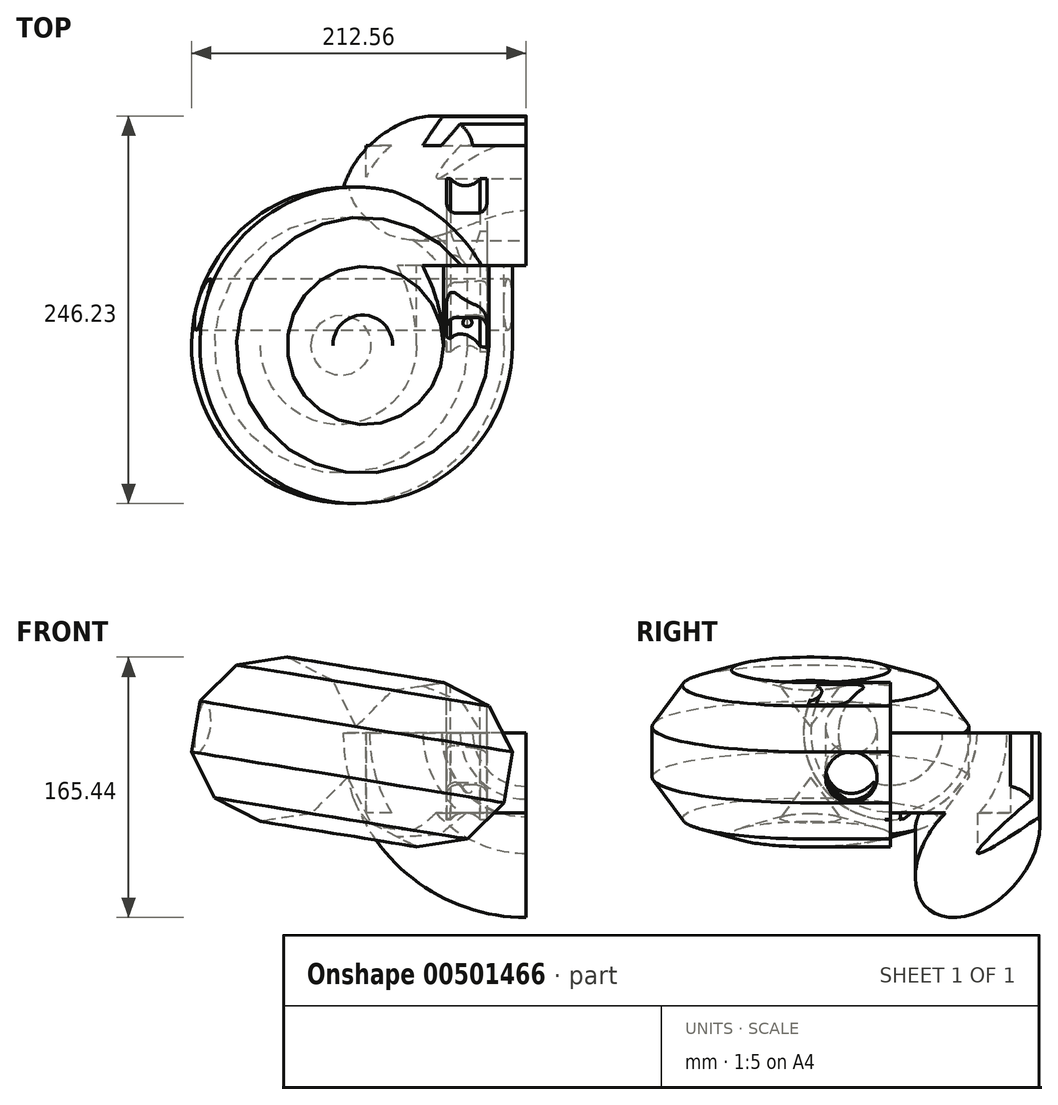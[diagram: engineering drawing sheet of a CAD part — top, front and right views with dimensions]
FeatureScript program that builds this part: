
annotation { "Feature Type Name" : "Feature", "Feature Type Description" : "" }
export const myFeature = defineFeature(function(context is Context, id is Id, definition is map)
    precondition{}
    {
        {
            var Q0;
            Q0=qCreatedBy(makeId("Right.planeOp"),FACE);
            var sketch = newSketch(context, id + "F0", { "sketchPlane" : qUnion([Q0])});
            skLineSegment(sketch, "E0.bottom", {"start": v(0, 50.8) * mm, "end": v(76.2, 50.8) * mm});
            skLineSegment(sketch, "E0.top", {"start": v(0, 0) * mm, "end": v(76.2, 0) * mm});
            skLineSegment(sketch, "E0.left", {"start": v(0, 50.8) * mm, "end": v(0, 0) * mm});
            skLineSegment(sketch, "E0.right", {"start": v(76.2, 50.8) * mm, "end": v(76.2, 0) * mm});
            skSolve(sketch);
        }
        {
            var Q0;
            Q0 = qSketchRegion(id + "F0", true);
            extrude(context, id + "F1", {"entities" : qUnion([Q0]), "depth" : 101.6 * mm});
        }
        {
            var Q0;
            Q0=makeQuery(id+"F1.opExtrude","CAP_FACE",FACE,{"disambiguationData":[OSD([sQuery(id+"F0.wireOp",EDGE,"E0.bottom"),sQuery(id+"F0.wireOp",EDGE,"E0.top"),sQuery(id+"F0.wireOp",EDGE,"E0.left"),sQuery(id+"F0.wireOp",EDGE,"E0.right")])],"isStart":false});
            var sketch = newSketch(context, id + "F2", { "sketchPlane" : qUnion([Q0])});
            skEllipticalArc(sketch, "E1", {});
            skEllipticalArc(sketch, "E2", {});
            skPoint(sketch, "E2.centerSnap0", {"position": v(55.38, -25.47) * mm});
            const initialGuessF2  = {"E1": [0.1582920104265213, 0.054269641637802124, -0.7904881080216445, -0.6124773882163822, 0.13018475622554335, 0.007689410792664507, 5.394513098691121, 0.8567772667814274], "E2": [0.05538250878453253, -0.0245770997165353, 0.6531900166199548, 0.7571940320604906, 0.048106603113153935, 0.03167227913565867, 6.147645044378101, 5.782845178718024]};
            skSetInitialGuess(sketch, initialGuessF2);
            skSolve(sketch);
        }
        {
            var Q0;
            {var subQ1=sQuery(id+"F2.wireOp",EDGE,"E1");Q0=makeQuery(id+"F2.imprint","IMPRINT",FACE,{"disambiguationData":[TD([[makeQuery(id+"F2.imprint","IMPRINT",EDGE,{"derivedFrom":subQ1}),-1.0]])]});}
            var Q1;
            Q1=makeQuery(id+"F1.opExtrude","CAP_EDGE",EDGE,{"disambiguationData":[OSD([sQuery(id+"F0.wireOp",EDGE,"E0.bottom")])],"isStart":false});
            revolve(context, id + "F3", {"operationType" : NewBodyOperationType.ADD, "entities" : qUnion([Q0]), "axis" : qUnion([Q1]), "revolveType" : RevolveType.ONE_DIRECTION, "angle" : 90 * degree});
        }
        {
            var Q0;
            Q0=makeQuery(id+"F1.opExtrude","SWEPT_FACE",FACE,{"disambiguationData":[OSD([sQuery(id+"F0.wireOp",EDGE,"E0.left")])]});
            var sketch = newSketch(context, id + "F4", { "sketchPlane" : qUnion([Q0])});
            skCircle(sketch, "E3.cCircle", {"center": v(40.49, 30.66) * mm, "radius": 52.85 * mm, "construction": true});
            skLineSegment(sketch, "E3.0", {"start": v(32, -21.5) * mm, "end": v(2.96, -6.55) * mm});
            skLineSegment(sketch, "E3.1", {"start": v(2.96, -6.55) * mm, "end": v(-11.74, 22.61) * mm});
            skLineSegment(sketch, "E3.2", {"start": v(-11.74, 22.61) * mm, "end": v(-6.5, 54.85) * mm});
            skLineSegment(sketch, "E3.3", {"start": v(-6.5, 54.85) * mm, "end": v(16.7, 77.85) * mm});
            skLineSegment(sketch, "E3.4", {"start": v(16.7, 77.85) * mm, "end": v(48.98, 82.82) * mm});
            skLineSegment(sketch, "E3.5", {"start": v(48.98, 82.82) * mm, "end": v(78.02, 67.87) * mm});
            skLineSegment(sketch, "E3.6", {"start": v(78.02, 67.87) * mm, "end": v(92.72, 38.7) * mm});
            skLineSegment(sketch, "E3.7", {"start": v(92.72, 38.7) * mm, "end": v(87.47, 6.46) * mm});
            skLineSegment(sketch, "E3.8", {"start": v(87.47, 6.46) * mm, "end": v(64.28, -16.53) * mm});
            skLineSegment(sketch, "E3.9", {"start": v(64.28, -16.53) * mm, "end": v(32, -21.5) * mm});
            skSolve(sketch);
        }
        {
            var Q0;
            Q0 = qSketchRegion(id + "F4", true);
            extrude(context, id + "F5", {"entities" : qUnion([Q0]), "operationType" : NewBodyOperationType.ADD, "depth" : 50.8 * mm});
        }
        {
            var Q0;
            Q0=makeQuery(id+"F5.opExtrude","CAP_FACE",FACE,{"disambiguationData":[OSD([sQuery(id+"F4.wireOp",EDGE,"E3.0"),sQuery(id+"F4.wireOp",EDGE,"E3.1"),sQuery(id+"F4.wireOp",EDGE,"E3.2"),sQuery(id+"F4.wireOp",EDGE,"E3.3"),sQuery(id+"F4.wireOp",EDGE,"E3.4"),sQuery(id+"F4.wireOp",EDGE,"E3.5"),sQuery(id+"F4.wireOp",EDGE,"E3.6"),sQuery(id+"F4.wireOp",EDGE,"E3.7"),sQuery(id+"F4.wireOp",EDGE,"E3.8"),sQuery(id+"F4.wireOp",EDGE,"E3.9")])],"isStart":false});
            var Q1;
            Q1=makeQuery(id+"F5.opExtrude","CAP_EDGE",EDGE,{"disambiguationData":[OSD([sQuery(id+"F4.wireOp",EDGE,"E3.2")])],"isStart":false});
            revolve(context, id + "F6", {"operationType" : NewBodyOperationType.ADD, "entities" : qUnion([Q0]), "axis" : qUnion([Q1]), "revolveType" : RevolveType.FULL});
        }
        {
            var Q0;
            Q0=makeQuery(id+"F5.opExtrude","SWEPT_FACE",FACE,{"disambiguationData":[OSD([sQuery(id+"F4.wireOp",EDGE,"E3.7")])]});
            var sketch = newSketch(context, id + "F7", { "sketchPlane" : qUnion([Q0])});
            skCircle(sketch, "E4", {"center": v(-24.83, 36.76) * mm, "radius": 16.33 * mm});
            skSolve(sketch);
        }
        {
            var Q0;
            Q0 = qSketchRegion(id + "F7", true);
            extrude(context, id + "F8", {"entities" : qUnion([Q0]), "operationType" : NewBodyOperationType.REMOVE, "endBound" : BoundingType.THROUGH_ALL, "oppositeDirection" : true, "depth" : 25.4 * mm});
        }
        {
            var Q0;
            Q0=makeQuery(id+"F3.boolean.opBoolean","MERGE",FACE,{"derivedFrom":[makeQuery(id+"F1.opExtrude","SWEPT_FACE",FACE,{"disambiguationData":[OSD([sQuery(id+"F0.wireOp",EDGE,"E0.bottom")])]}),makeQuery(id+"F3.opRevolve","CAP_FACE",FACE,{"disambiguationData":[OSD([sQuery(id+"F0.wireOp",EDGE,"E0.top"),sQuery(id+"F0.wireOp",EDGE,"E0.right"),sQuery(id+"F2.wireOp",EDGE,"E1"),sQuery(id+"F2.wireOp",EDGE,"E2")])],"isStart":false})]});
            var sketch = newSketch(context, id + "F9", { "sketchPlane" : qUnion([Q0])});
            skLineSegment(sketch, "E5.bottom", {"start": v(70.31, 33.13) * mm, "end": v(57.4, 33.13) * mm});
            skLineSegment(sketch, "E5.top", {"start": v(76.66, 55.18) * mm, "end": v(72.33, 55.18) * mm});
            skLineSegment(sketch, "E5.left", {"start": v(76.66, 39.48) * mm, "end": v(76.66, 55.18) * mm});
            skLineSegment(sketch, "E5.right", {"start": v(51.04, 39.48) * mm, "end": v(51.04, 55.18) * mm});
            skArc(sketch, "E6", {"start": v(53.65, 55.18) * mm, "mid": v(62.99, 50.56) * mm, "end": v(72.33, 55.18) * mm});
            skPoint(sketch, "E7.visualSharp", {"position": v(51.04, 33.13) * mm});
            skArc(sketch, "E7.filletArc", {"start": v(51.04, 39.48) * mm, "mid": v(52.9, 35) * mm, "end": v(57.4, 33.13) * mm});
            skPoint(sketch, "E8.visualSharp", {"position": v(76.66, 33.13) * mm});
            skArc(sketch, "E8.filletArc", {"start": v(70.31, 33.13) * mm, "mid": v(74.8, 35) * mm, "end": v(76.66, 39.48) * mm});
            skLineSegment(sketch, "E9.trimOffspring", {"start": v(53.65, 55.18) * mm, "end": v(51.04, 55.18) * mm});
            skSolve(sketch);
        }
        {
            var Q0;
            Q0 = qSketchRegion(id + "F9", true);
            var Q1;
            {var subQ0=sQuery(id+"F0.wireOp",EDGE,"E0.bottom");var subQ1=sQuery(id+"F0.wireOp",EDGE,"E0.left");Q1=makeQuery(id+"F5.boolean.opBoolean","SPLIT",EDGE,{"disambiguationData":[topologyDisambiguationEdgeConnected([makeQuery(id+"F1.opExtrude","SWEPT_FACE",FACE,{"disambiguationData":[OSD([subQ1])]})])],"derivedFrom":makeQuery(id+"F1.opExtrude","SWEPT_EDGE",EDGE,{"disambiguationData":[OSD([subQ0,subQ1])]})});}
            revolve(context, id + "F10", {"operationType" : NewBodyOperationType.REMOVE, "entities" : qUnion([Q0]), "axis" : qUnion([Q1]), "revolveType" : RevolveType.FULL, "oppositeDirection" : true});
        }
    });
